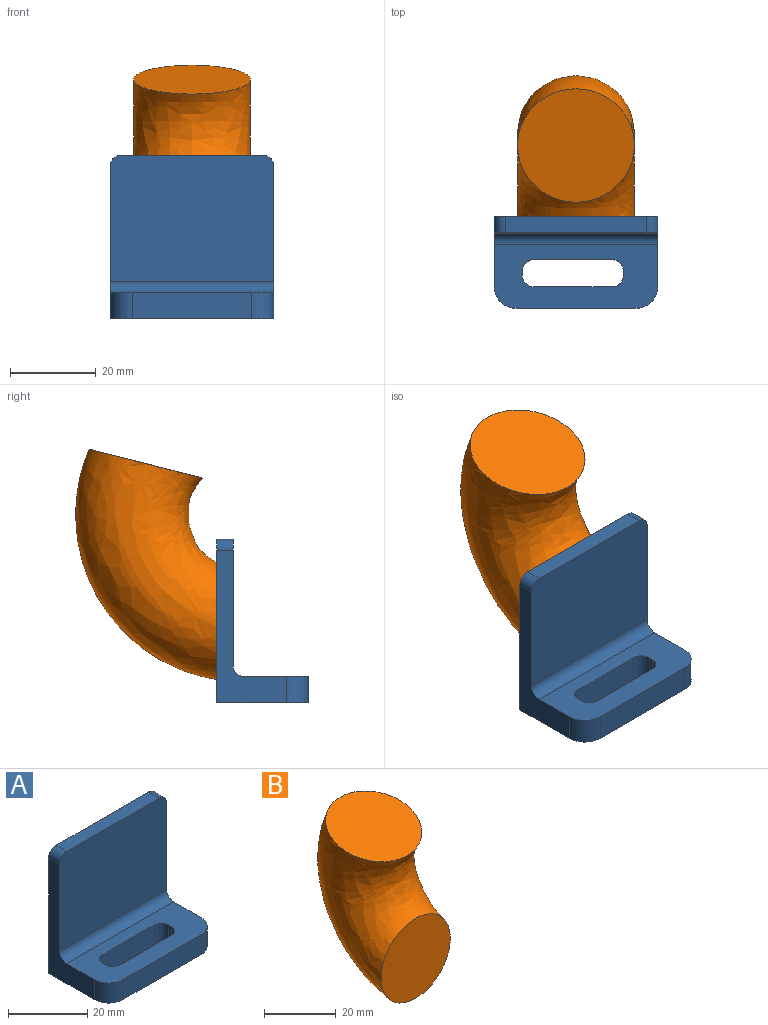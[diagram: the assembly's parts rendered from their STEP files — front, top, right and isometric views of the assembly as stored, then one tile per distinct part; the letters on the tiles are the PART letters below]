
ASSEMBLY  parts=2 mates=1
PART A: 21 faces, bbox 38.1x21.3x38.1 mm
  f0: plane 38.1x29.42mm, normal (0,-1,0), area 1117.9mm2, adj f1,f2,f4,f6,f7,f10
  f1: plane 33.02x3.81mm, normal (0,0,1), area 125.8mm2, adj f0,f5,f6,f7
  f2: plane 35.56x16.26mm, normal (-1,0,0), area 213.4mm2, adj f0,f3,f5,f6,f8,f10,f19
  f3: plane 38.1x21.34mm, normal (0,0,-1), area 659.6mm2, adj f2,f4,f5,f9,f11,f12,f13,f14
  f4: plane 35.56x16.26mm, normal (1,0,0), area 213.4mm2, adj f0,f3,f5,f7,f8,f10,f20
  f5: plane 38.1x38.1mm, normal (0,1,0), area 1448.8mm2, adj f1,f2,f3,f4,f6,f7
  f6: cylinder r=2.54mm len=3.81mm, axis (0,-1,0), area 15.2mm2, adj f0,f1,f2,f5
  f7: cylinder r=2.54mm len=3.81mm, axis (0,1,0), area 15.2mm2, adj f0,f1,f4,f5
  f8: plane 38.1x14.99mm, normal (0,0,1), area 417.7mm2, adj f2,f4,f9,f10,f11,f12,f13,f14
  f9: plane 27.94x6.15mm, normal (0,-1,0), area 171.7mm2, adj f3,f8,f19,f20
  f10: cylinder r=2.54mm len=38.1mm, axis (-1,0,0), area 152mm2, adj f0,f2,f4,f8
  f11: plane 6.15x1.21mm, normal (-1,0,0), area 7.5mm2, adj f3,f8,f12,f18
  f12: cylinder r=2.54mm len=6.15mm, axis (0,0,1), area 24.5mm2, adj f3,f8,f11,f13
  f13: plane 18.39x6.15mm, normal (0,-1,0), area 113mm2, adj f3,f8,f12,f14
  f14: cylinder r=2.54mm len=6.15mm, axis (0,0,1), area 24.5mm2, adj f3,f8,f13,f15
  f15: plane 6.15x1.21mm, normal (1,0,0), area 7.5mm2, adj f3,f8,f14,f16
  f16: cylinder r=2.54mm len=6.15mm, axis (0,0,1), area 24.5mm2, adj f3,f8,f15,f17
  f17: plane 18.39x6.15mm, normal (0,1,0), area 113mm2, adj f3,f8,f16,f18
  f18: cylinder r=2.54mm len=6.15mm, axis (0,0,1), area 24.5mm2, adj f3,f8,f11,f17
  f19: cylinder r=5.08mm len=6.15mm, axis (0,0,1), area 49mm2, adj f2,f3,f8,f9
  f20: cylinder r=5.08mm len=6.15mm, axis (0,0,-1), area 49mm2, adj f3,f4,f8,f9
PART B: 3 faces, bbox 54.4x40.6x53.7 mm
  f0: plane 27.22x27.22mm, normal (0,-1,0), area 581.9mm2, adj f2
  f1: plane 27.22x26.37mm, normal (0,-0.25,0.97), area 581.9mm2, adj f2
  f2: bspline ~54.44x53.68mm, area 3931.8mm2, adj f0,f1
PLACE A t=(1.87,29.92,-1.3)mm
PLACE B t=(2.62,29.92,35.76)mm
MATE fastened A.f5 <-> B.f0  axis (0,1,0) through (2.62,29.92,-0.91)mm
